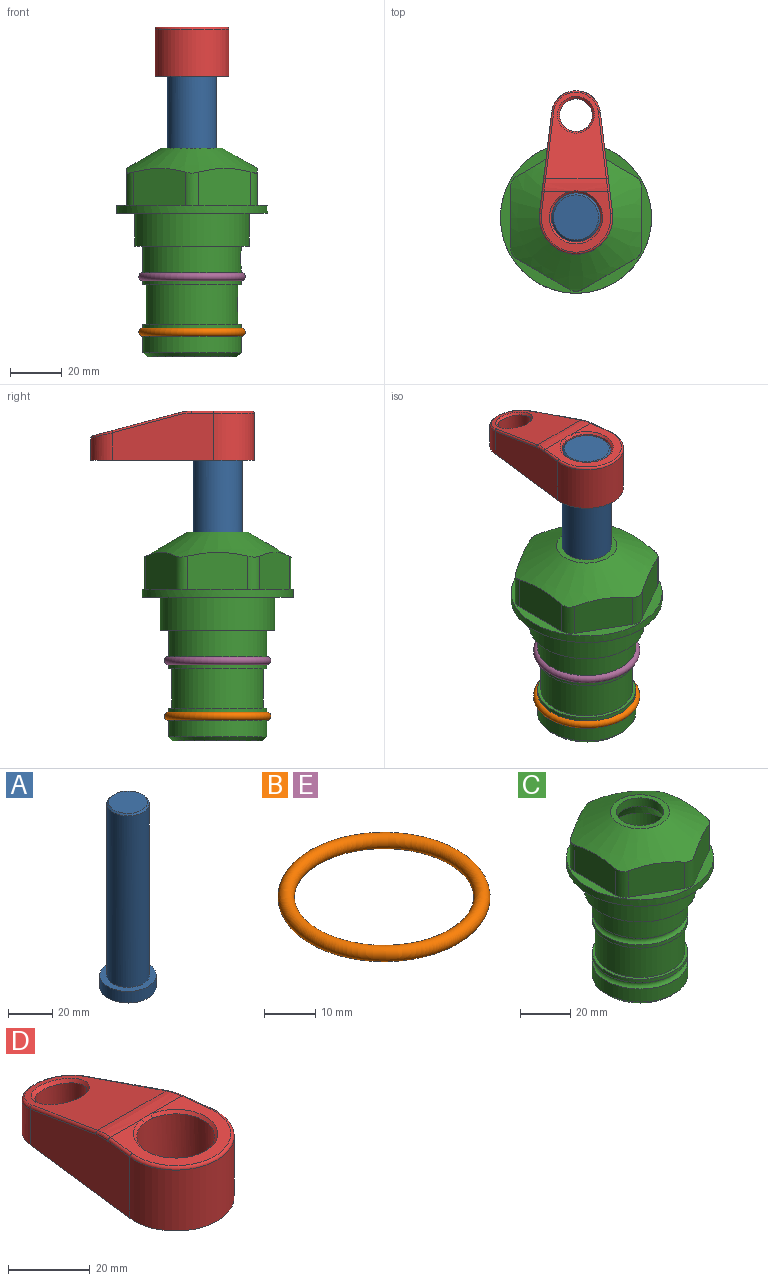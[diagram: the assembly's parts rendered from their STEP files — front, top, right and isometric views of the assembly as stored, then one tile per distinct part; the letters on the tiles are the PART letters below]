
ASSEMBLY  parts=5 mates=4
PART A: 6 faces, bbox 25.4x25.4x101.6 mm
  f0: plane 17.46x17.46mm, normal (0,0,1), area 239.5mm2, adj f5
  f1: plane 25.4x25.4mm, normal (0,0,-1), area 506.7mm2, adj f2
  f2: cylinder r=12.7mm len=25.4mm, axis (0,0,1), area 506.7mm2, adj f1,f3
  f3: plane 25.4x25.4mm, normal (0,0,1), area 221.7mm2, adj f2,f4
  f4: cylinder r=9.53mm len=94.46mm, axis (0,0,1), area 5653mm2, adj f3,f5
  f5: cone r=8.73mm half-angle=45deg, axis (0,0,-1), area 64.4mm2, adj f0,f4
PART B: 1 faces, bbox 44.7x44.7x3.2 mm
  f0: torus R=19.05mm, axis (0,0,1), area 1193.9mm2
PART C: 36 faces, bbox 58.7x58.7x81 mm
  f0: cylinder r=17.78mm len=35.56mm, axis (0,0,1), area 1670.8mm2, adj f23,f24,f31
  f1: cylinder r=19.05mm len=38.1mm, axis (0,0,1), area 1191.9mm2, adj f26,f27,f30
  f2: plane 58.66x58.66mm, normal (0,0,-1), area 1150.6mm2, adj f3,f28
  f3: cylinder r=29.33mm len=58.66mm, axis (0,0,-1), area 585.1mm2, adj f2,f4
  f4: plane 58.66x58.66mm, normal (0,0,1), area 475.9mm2, adj f3,f5,f6,f7,f8,f9,f10,f11
  f5: plane 20.32x14.34mm, normal (-0.5,0.87,0), area 324.4mm2, adj f4,f15,f16,f17
  f6: plane 20.32x14.34mm, normal (0.5,0.87,0), area 324.4mm2, adj f4,f14,f15,f17
  f7: plane 23.48x14.34mm, normal (1,0,0), area 324.4mm2, adj f4,f13,f14,f17
  f8: plane 20.32x14.34mm, normal (0.5,-0.87,0), area 324.4mm2, adj f4,f12,f13,f17
  f9: plane 20.32x14.34mm, normal (-0.5,-0.87,0), area 324.4mm2, adj f4,f11,f12,f17
  f10: plane 23.48x14.34mm, normal (-1,0,0), area 324.4mm2, adj f4,f11,f16,f17
  f11: cylinder r=5.08mm len=12.85mm, axis (0,0,-1), area 67.2mm2, adj f4,f9,f10,f17
  f12: cylinder r=5.08mm len=12.85mm, axis (0,0,-1), area 67.2mm2, adj f4,f8,f9,f17
  f13: cylinder r=5.08mm len=12.85mm, axis (0,0,-1), area 67.2mm2, adj f4,f7,f8,f17
  f14: cylinder r=5.08mm len=12.85mm, axis (0,0,-1), area 67.2mm2, adj f4,f6,f7,f17
  f15: cylinder r=5.08mm len=12.85mm, axis (0,0,-1), area 67.2mm2, adj f4,f5,f6,f17
  f16: cylinder r=5.08mm len=12.85mm, axis (0,0,-1), area 67.2mm2, adj f4,f5,f10,f17
  f17: cone r=11.73mm half-angle=60deg, axis (0,0,-1), area 2071.8mm2, adj f5,f6,f7,f8,f9,f10,f11,f12
  f18: plane 23.46x23.46mm, normal (0,0,1), area 147.4mm2, adj f17,f35
  f19: plane 34.93x34.93mm, normal (0,0,-1), area 958mm2, adj f29
  f20: cylinder r=19.05mm len=38.1mm, axis (0,0,1), area 760.1mm2, adj f21,f29
  f21: torus R=19.05mm, axis (0,0,1), area 565.3mm2, adj f20,f22
  f22: cylinder r=19.05mm len=38.1mm, axis (0,0,1), area 190mm2, adj f21,f23
  f23: plane 38.1x38.1mm, normal (0,0,1), area 146.9mm2, adj f0,f22
  f24: plane 38.1x38.1mm, normal (0,0,-1), area 146.9mm2, adj f0,f25
  f25: cylinder r=19.05mm len=38.1mm, axis (0,0,1), area 190mm2, adj f24,f26
  f26: torus R=19.05mm, axis (0,0,1), area 565.3mm2, adj f1,f25
  f27: plane 44.45x44.45mm, normal (0,0,-1), area 411.7mm2, adj f1,f28
  f28: cylinder r=22.23mm len=44.45mm, axis (0,0,1), area 1773.5mm2, adj f2,f27
  f29: cone r=19.05mm half-angle=45deg, axis (0,0,1), area 257.5mm2, adj f19,f20
  f30: cylinder r=3.17mm len=6.75mm, axis (-1,0,0), area 128mm2, adj f1,f33
  f31: cylinder r=3.17mm len=6.35mm, axis (-1,0,0), area 102.5mm2, adj f0,f33
  f32: plane 25.4x25.4mm, normal (0,0,1), area 506.7mm2, adj f33
  f33: cylinder r=12.7mm len=66.42mm, axis (0,0,-1), area 5236.2mm2, adj f30,f31,f32,f34
  f34: cone r=9.53mm half-angle=30deg, axis (0,0,-1), area 443.4mm2, adj f33,f35
  f35: cylinder r=9.53mm len=19.05mm, axis (0,0,-1), area 240.9mm2, adj f18,f34
PART D: 31 faces, bbox 31.7x65.5x19.8 mm
  f0: plane 39.12x18.26mm, normal (0.99,0.12,0), area 612.2mm2, adj f1,f4,f7,f11,f13,f15
  f1: cylinder r=9.53mm len=18.91mm, axis (0,0,-1), area 296.1mm2, adj f0,f2,f7,f17
  f2: plane 39.12x18.26mm, normal (-0.99,0.12,0), area 612.2mm2, adj f1,f4,f7,f12,f14,f16
  f3: cylinder r=6.35mm len=12.7mm, axis (0,0,-1), area 362.4mm2, adj f7,f18
  f4: cylinder r=14.29mm len=28.58mm, axis (0,0,-1), area 882.2mm2, adj f0,f2,f7,f10
  f5: cylinder r=9.53mm len=19.05mm, axis (0,0,-1), area 1092.6mm2, adj f7,f19,f20
  f6: plane 26.99x23.69mm, normal (0,0,1), area 216.2mm2, adj f9,f10,f11,f12,f19
  f7: plane 63.5x28.58mm, normal (0,0,-1), area 661.8mm2, adj f0,f1,f2,f3,f4,f5,f22,f23
  f8: plane 33.52x23.6mm, normal (0,0.26,0.97), area 486mm2, adj f9,f15,f16,f17,f18
  f9: cylinder r=19.05mm len=24.72mm, axis (1,0,0), area 120.4mm2, adj f6,f8,f13,f14,f20
  f10: torus R=13.49mm, axis (0,0,1), area 59mm2, adj f4,f6,f11,f12
  f11: cylinder r=0.79mm len=8.67mm, axis (0.12,-0.99,0), area 10.8mm2, adj f0,f6,f10,f13
  f12: cylinder r=0.79mm len=8.67mm, axis (0.12,0.99,0), area 10.8mm2, adj f2,f6,f10,f14
  f13: bspline ~4.95x1.42mm, area 6.1mm2, adj f0,f9,f11,f15
  f14: bspline ~4.95x1.42mm, area 6.1mm2, adj f2,f9,f12,f16
  f15: cylinder r=0.79mm len=25.95mm, axis (0.12,-0.96,0.26), area 32.9mm2, adj f0,f8,f13,f17
  f16: cylinder r=0.79mm len=25.95mm, axis (0.12,0.96,-0.26), area 32.9mm2, adj f2,f8,f14,f17
  f17: bspline ~18.91x8.38mm, area 30mm2, adj f1,f8,f15,f16
  f18: bspline ~14.29x14.29mm, area 48.3mm2, adj f3,f8
  f19: cone r=9.53mm half-angle=45deg, axis (0,0,1), area 66.5mm2, adj f5,f6,f20
  f20: bspline ~3.22x0.96mm, area 3.5mm2, adj f5,f9,f19
  f21: plane 2.75x2.72mm, normal (0,0,-1), area 2.9mm2, adj f23,f25,f28
  f22: plane 23.05x15.88mm, normal (-0.99,-0.12,0), area 323.6mm2, adj f7,f25,f26,f27,f28,f29
  f23: plane 23.05x15.88mm, normal (0.99,-0.12,0), area 323.6mm2, adj f7,f21,f25,f27,f28,f30
  f24: cylinder r=9.53mm len=10.69mm, axis (0,0,-1), area 114.7mm2, adj f7,f27,f29,f30
  f25: cylinder r=12.7mm len=20.59mm, axis (0,0,-1), area 381.1mm2, adj f7,f21,f22,f23,f26,f28
  f26: plane 2.75x2.72mm, normal (0,0,-1), area 2.9mm2, adj f22,f25,f28
  f27: plane 19.72x18.37mm, normal (0,-0.26,-0.97), area 291.8mm2, adj f22,f23,f24,f28,f29,f30
  f28: cylinder r=15.88mm len=19.92mm, axis (1,0,0), area 54.8mm2, adj f21,f22,f23,f25,f26,f27
  f29: cylinder r=1.59mm len=11mm, axis (0,0,-1), area 34.7mm2, adj f7,f22,f24,f27
  f30: cylinder r=1.59mm len=11mm, axis (0,0,-1), area 34.7mm2, adj f7,f23,f24,f27
PART E: same geometry as B
PLACE A rot(axis=(0,0,1),0deg) t=(45.52,-43.43,29.79)mm
PLACE B t=(45.52,-43.43,0.2)mm
PLACE C t=(45.52,-43.43,21.79)mm
PLACE D rot(axis=(0,0,1),0deg) t=(45.52,-43.43,30.59)mm
PLACE E t=(45.52,-43.43,21.79)mm
MATE cylindrical A.f2 <-> B.f0  axis (0,0,-1) through (45.52,-43.43,-8.31)mm
MATE fastened B.f0 <-> C.f0  axis (0,0,1) through (45.52,-43.43,-24.31)mm
MATE fastened D.f4 <-> A.f2  axis (0,0,-1) through (45.52,-43.43,93.29)mm
MATE fastened E.f0 <-> C.f0  axis (0,0,1) through (45.52,-43.43,-2.72)mm
